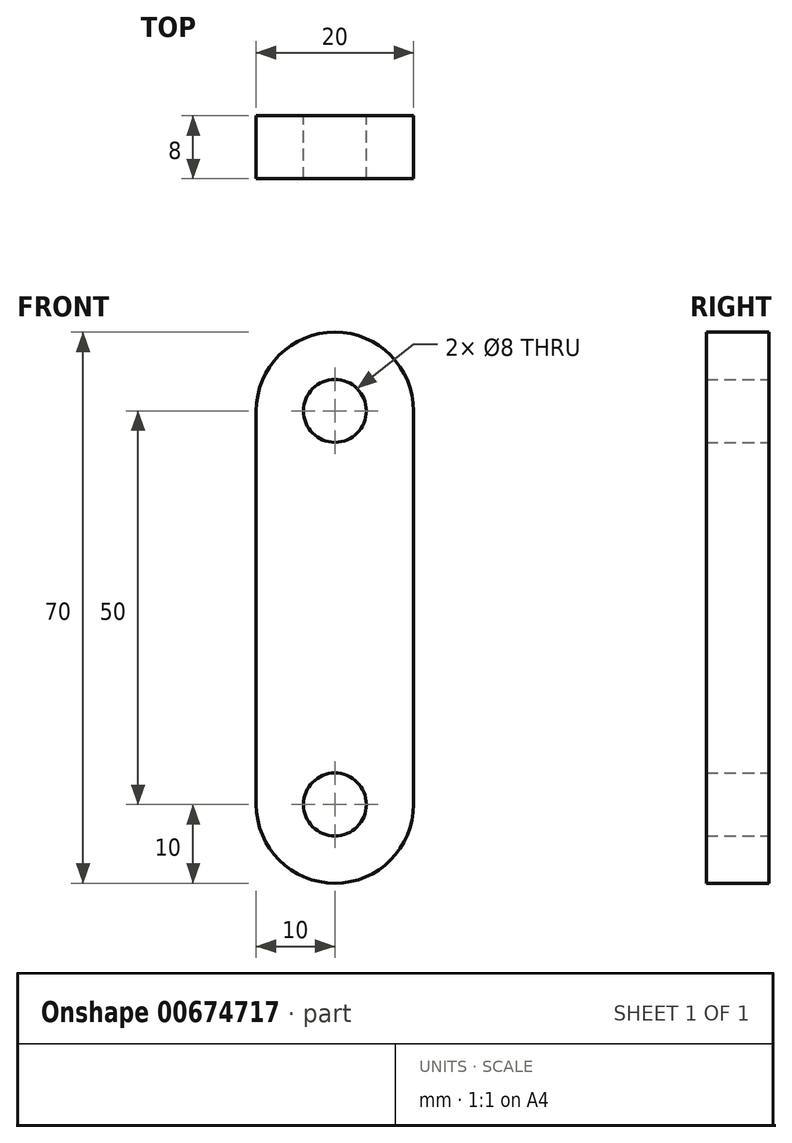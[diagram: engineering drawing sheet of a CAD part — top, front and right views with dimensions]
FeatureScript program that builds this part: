
annotation { "Feature Type Name" : "Feature", "Feature Type Description" : "" }
export const myFeature = defineFeature(function(context is Context, id is Id, definition is map)
    precondition{}
    {
        {
            var Q0;
            Q0=qCreatedBy(makeId("Front.planeOp"),FACE);
            var sketch = newSketch(context, id + "F0", { "sketchPlane" : qUnion([Q0])});
            skCircle(sketch, "E0", {"center": v(0, 0) * mm, "radius": 10 * mm});
            skCircle(sketch, "E1", {"center": v(0, 50) * mm, "radius": 10 * mm});
            skCircle(sketch, "E2", {"center": v(0, 50) * mm, "radius": 4 * mm});
            skCircle(sketch, "E3", {"center": v(0, 0) * mm, "radius": 4 * mm});
            skLineSegment(sketch, "E4", {"start": v(-10, 50) * mm, "end": v(-10, 0) * mm});
            skLineSegment(sketch, "E5", {"start": v(10, 50) * mm, "end": v(10, 0) * mm});
            skSolve(sketch);
        }
        {
            var Q0;
            Q0 = qSketchRegion(id + "F0", true);
            extrude(context, id + "F1", {"entities" : qUnion([Q0]), "depth" : 8 * mm, "offsetDistance" : 25 * mm});
        }
    });
